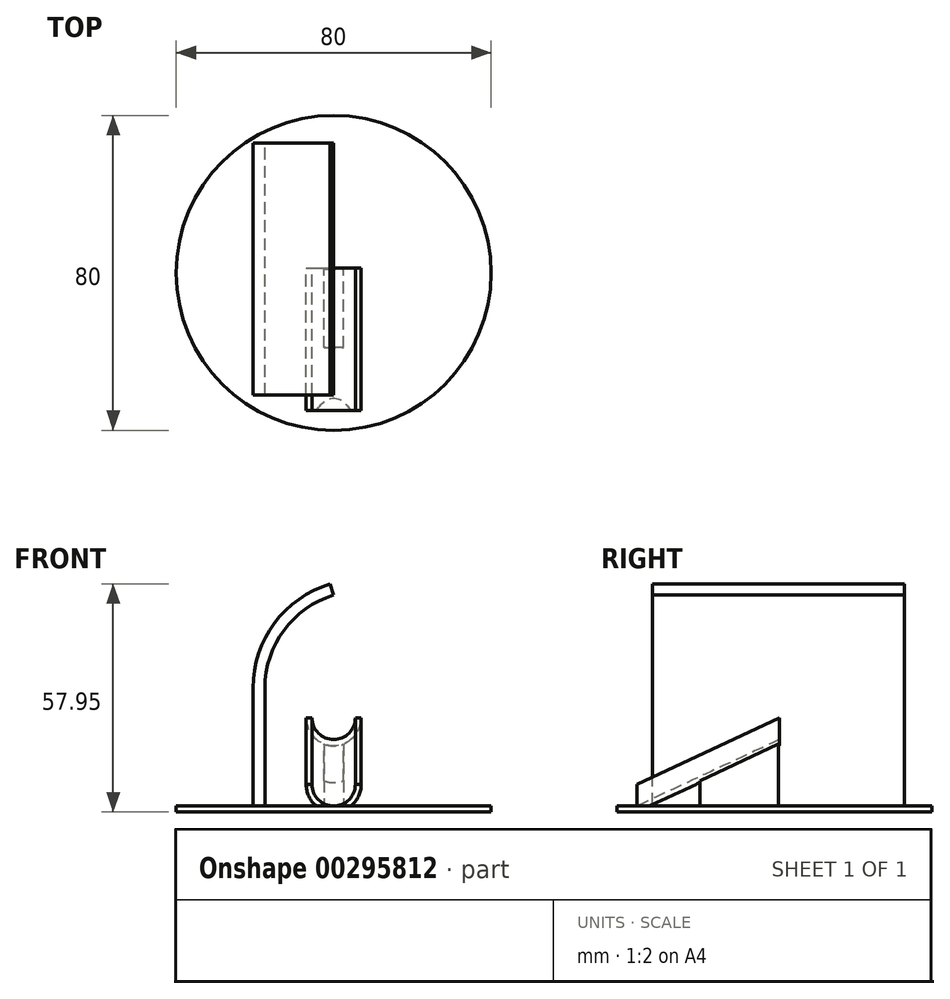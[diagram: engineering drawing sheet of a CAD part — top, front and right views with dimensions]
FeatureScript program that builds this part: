
annotation { "Feature Type Name" : "Feature", "Feature Type Description" : "" }
export const myFeature = defineFeature(function(context is Context, id is Id, definition is map)
    precondition{}
    {
        {
            var Q0;
            Q0=qCreatedBy(makeId("Front.planeOp"),FACE);
            var sketch = newSketch(context, id + "F0", { "sketchPlane" : qUnion([Q0])});
            skLineSegment(sketch, "E0", {"start": v(-13.2, 7) * mm, "end": v(13.48, 7) * mm, "construction": true});
            skPoint(sketch, "E1", {"position": v(-7, 7) * mm});
            skPoint(sketch, "E2", {"position": v(7, 7) * mm});
            skArc(sketch, "E3", {"start": v(-7, 7) * mm, "mid": v(0, 0) * mm, "end": v(7, 7) * mm});
            skPoint(sketch, "E4", {"position": v(-5.5, 7) * mm});
            skPoint(sketch, "E5", {"position": v(5.5, 7) * mm});
            skArc(sketch, "E6", {"start": v(-5.5, 7) * mm, "mid": v(0, 1.5) * mm, "end": v(5.5, 7) * mm});
            skLineSegment(sketch, "E7", {"start": v(-7, 7) * mm, "end": v(-5.5, 7) * mm});
            skLineSegment(sketch, "E8", {"start": v(5.5, 7) * mm, "end": v(7, 7) * mm});
            skSolve(sketch);
        }
        {
            var Q0;
            Q0=qCreatedBy(makeId("Right.planeOp"),FACE);
            var sketch = newSketch(context, id + "F1", { "sketchPlane" : qUnion([Q0])});
            skLineSegment(sketch, "E9", {"start": v(0, 0) * mm, "end": v(36.25, 16.9) * mm});
            skSolve(sketch);
        }
        {
            var Q0;
            Q0=makeQuery(id+"F0.imprint","IMPRINT",FACE,{"disambiguationData":[TD([[makeQuery(id+"F0.imprint","IMPRINT",EDGE,{"derivedFrom":sQuery(id+"F0.wireOp",EDGE,"E3")}),1.0]])]});
            var Q1;
            Q1=sQuery(id+"F1.wireOp",EDGE,"E9");
            sweep(context, id + "F2", {"profiles" : qUnion([Q0]), "path" : qUnion([Q1])});
        }
        {
            var Q0;
            Q0=qCreatedBy(makeId("Top.planeOp"),FACE);
            var sketch = newSketch(context, id + "F3", { "sketchPlane" : qUnion([Q0])});
            skCircle(sketch, "E10", {"center": v(0, 35) * mm, "radius": 40 * mm});
            skLineSegment(sketch, "E11.bottom", {"start": v(2.5, 36) * mm, "end": v(-2.5, 36) * mm});
            skLineSegment(sketch, "E11.top", {"start": v(2.5, 16) * mm, "end": v(-2.5, 16) * mm});
            skLineSegment(sketch, "E11.left", {"start": v(2.5, 36) * mm, "end": v(2.5, 16) * mm});
            skLineSegment(sketch, "E11.right", {"start": v(-2.5, 36) * mm, "end": v(-2.5, 16) * mm});
            skSolve(sketch);
        }
        {
            var Q0;
            Q0=makeQuery(id+"F3.imprint","IMPRINT",FACE,{"disambiguationData":[TD([[makeQuery(id+"F3.imprint","IMPRINT",EDGE,{"derivedFrom":sQuery(id+"F3.wireOp",EDGE,"E11.bottom")}),1.0]])]});
            var Q1;
            Q1=makeQuery(id+"F2.opSweep","SWEPT_FACE",FACE,{"disambiguationData":[OSD([sQuery(id+"F0.wireOp",EDGE,"E3"),sQuery(id+"F1.wireOp",EDGE,"E9")])]});
            extrude(context, id + "F4", {"entities" : qUnion([Q0]), "operationType" : NewBodyOperationType.ADD, "endBound" : BoundingType.UP_TO_SURFACE, "endBoundEntityFace" : qUnion([Q1]), "depth" : 25 * mm});
        }
        {
            var Q0;
            Q0 = qSketchRegion(id + "F3", true);
            extrude(context, id + "F5", {"entities" : qUnion([Q0]), "operationType" : NewBodyOperationType.ADD, "depth" : 1.5 * mm});
        }
        {
            var Q0;
            Q0=makeQuery(id+"F5.opExtrude","CAP_FACE",FACE,{"disambiguationData":[OSD([sQuery(id+"F3.wireOp",EDGE,"E10"),sQuery(id+"F3.wireOp",EDGE,"E11.bottom"),sQuery(id+"F3.wireOp",EDGE,"E11.top"),sQuery(id+"F3.wireOp",EDGE,"E11.left"),sQuery(id+"F3.wireOp",EDGE,"E11.right")])],"isStart":false});
            var sketch = newSketch(context, id + "F6", { "sketchPlane" : qUnion([Q0])});
            skLineSegment(sketch, "E12.bottom", {"start": v(-17.49, 4) * mm, "end": v(-20.49, 4) * mm});
            skLineSegment(sketch, "E12.top", {"start": v(-17.49, 68) * mm, "end": v(-20.49, 68) * mm});
            skLineSegment(sketch, "E12.left", {"start": v(-17.49, 4) * mm, "end": v(-17.49, 68) * mm});
            skLineSegment(sketch, "E12.right", {"start": v(-20.49, 4) * mm, "end": v(-20.49, 68) * mm});
            skSolve(sketch);
        }
        {
            var Q0;
            Q0=qCreatedBy(makeId("Front.planeOp"),FACE);
            var Q1;
            Q1=sQuery(id+"F6.wireOp",VERTEX,"E12.left.end");
            cPlane(context, id + "F7", {"entities" : qUnion([Q0, Q1]), "cplaneType" : CPlaneType.PLANE_POINT, "offset" : 25 * mm, "oppositeDirection" : true, "width" : 150 * mm, "height" : 150 * mm});
        }
        {
            var Q0;
            Q0=qCreatedBy(id+"F7.planeOp",FACE);
            var sketch = newSketch(context, id + "F8", { "sketchPlane" : qUnion([Q0])});
            skPoint(sketch, "E13.0", {"position": v(-17.49, 1.5) * mm});
            skLineSegment(sketch, "E14", {"start": v(-17.49, 1.5) * mm, "end": v(-17.49, 31.5) * mm});
            skArc(sketch, "E15", {"start": v(0, 55.08) * mm, "mid": v(-12.64, 46.18) * mm, "end": v(-17.49, 31.5) * mm});
            skSolve(sketch);
        }
        {
            var Q0;
            Q0=makeQuery(id+"F6.imprint","IMPRINT",FACE,{"disambiguationData":[TD([[makeQuery(id+"F6.imprint","IMPRINT",EDGE,{"derivedFrom":sQuery(id+"F6.wireOp",EDGE,"E12.bottom")}),-1.0]])]});
            var Q1;
            Q1=sQuery(id+"F8.wireOp",EDGE,"E14");
            var Q2;
            Q2=sQuery(id+"F8.wireOp",EDGE,"E15");
            sweep(context, id + "F9", {"operationType" : NewBodyOperationType.ADD, "profiles" : qUnion([Q0]), "path" : qUnion([Q1, Q2])});
        }
    });
